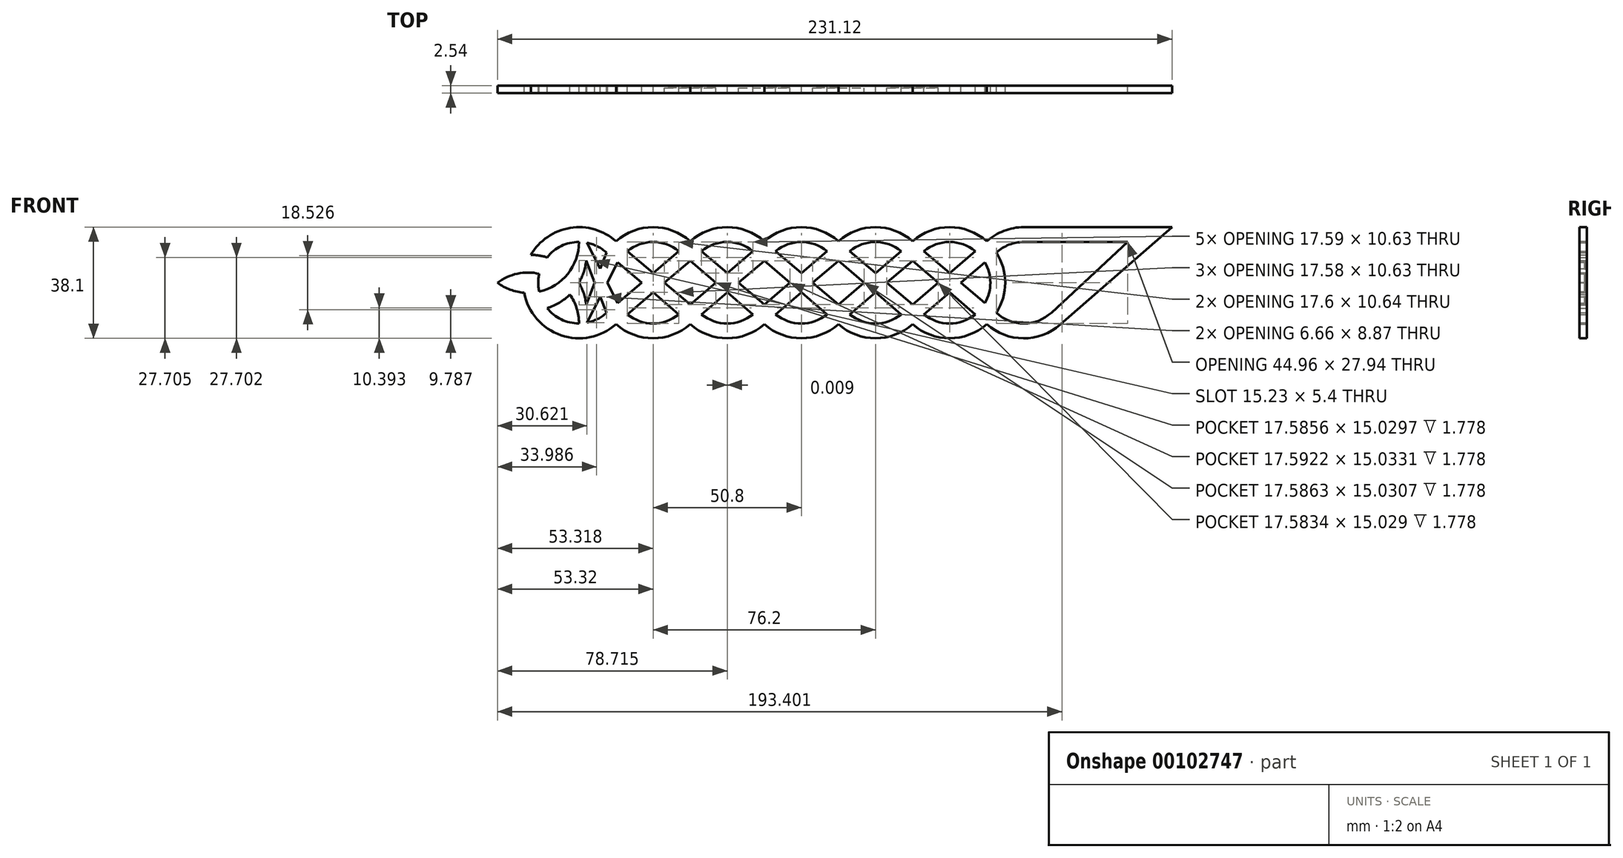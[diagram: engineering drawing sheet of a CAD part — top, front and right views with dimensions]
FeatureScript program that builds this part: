
annotation { "Feature Type Name" : "Feature", "Feature Type Description" : "" }
export const myFeature = defineFeature(function(context is Context, id is Id, definition is map)
    precondition{}
    {
        {
            var Q0;
            Q0=qCreatedBy(makeId("Front.planeOp"),FACE);
            var sketch = newSketch(context, id + "F3", { "sketchPlane" : qUnion([Q0])});
            skPoint(sketch, "E0", {"position": v(0, 0) * mm});
            skLineSegment(sketch, "E1.bottom", {"start": v(0, 0) * mm, "end": v(0, 0) * mm});
            skLineSegment(sketch, "E1.top", {"start": v(0, 0) * mm, "end": v(0, 0) * mm});
            skLineSegment(sketch, "E1.left", {"start": v(0, 0) * mm, "end": v(0, 0) * mm});
            skLineSegment(sketch, "E1.right", {"start": v(0, 0) * mm, "end": v(0, 0) * mm});
            skLineSegment(sketch, "E2.bottom", {"start": v(76.2, 19.05) * mm, "end": v(-76.2, 19.05) * mm, "construction": true});
            skLineSegment(sketch, "E2.top", {"start": v(76.2, -19.05) * mm, "end": v(-76.2, -19.05) * mm, "construction": true});
            skPoint(sketch, "E3", {"position": v(-76.2, 19.05) * mm});
            skPoint(sketch, "E4", {"position": v(76.2, 19.05) * mm});
            skPoint(sketch, "E5", {"position": v(76.2, -19.05) * mm});
            skPoint(sketch, "E6", {"position": v(-76.2, -19.05) * mm});
            skPoint(sketch, "E7", {"position": v(-76.2, 13.97) * mm});
            skPoint(sketch, "E8", {"position": v(-76.2, -13.97) * mm});
            skPoint(sketch, "E9", {"position": v(76.2, -13.97) * mm});
            skPoint(sketch, "E10", {"position": v(-50.8, 19.05) * mm});
            skPoint(sketch, "E11", {"position": v(-25.4, 19.05) * mm});
            skPoint(sketch, "E12", {"position": v(0, 19.05) * mm});
            skPoint(sketch, "E13", {"position": v(25.4, 19.05) * mm});
            skPoint(sketch, "E14", {"position": v(50.8, 19.05) * mm});
            skPoint(sketch, "E15", {"position": v(-50.8, 13.97) * mm});
            skPoint(sketch, "E16", {"position": v(-25.4, 13.97) * mm});
            skPoint(sketch, "E17", {"position": v(0, 13.97) * mm});
            skPoint(sketch, "E18", {"position": v(25.4, 13.97) * mm});
            skPoint(sketch, "E19", {"position": v(50.8, 13.97) * mm});
            skPoint(sketch, "E20", {"position": v(76.2, 13.97) * mm});
            skLineSegment(sketch, "E21", {"start": v(-76.2, 0) * mm, "end": v(-54.7, 0) * mm, "construction": true});
            skPoint(sketch, "E22", {"position": v(-76.2, 0) * mm});
            skPoint(sketch, "E23", {"position": v(76.2, 0) * mm});
            skPoint(sketch, "E24.MirrorP", {"position": v(-50.8, -19.05) * mm});
            skPoint(sketch, "E25.MirrorP", {"position": v(-50.8, -13.97) * mm});
            skPoint(sketch, "E26.MirrorP", {"position": v(-25.4, -19.05) * mm});
            skPoint(sketch, "E27.MirrorP", {"position": v(-25.4, -13.97) * mm});
            skPoint(sketch, "E28.MirrorP", {"position": v(0, -19.05) * mm});
            skPoint(sketch, "E29.MirrorP", {"position": v(0, -13.97) * mm});
            skPoint(sketch, "E30.MirrorP", {"position": v(25.4, -13.97) * mm});
            skPoint(sketch, "E31.MirrorP", {"position": v(25.4, -19.05) * mm});
            skPoint(sketch, "E32.MirrorP", {"position": v(50.8, -13.97) * mm});
            skPoint(sketch, "E33.MirrorP", {"position": v(50.8, -19.05) * mm});
            skPoint(sketch, "E34", {"position": v(-50.8, 0) * mm});
            skPoint(sketch, "E35", {"position": v(-25.4, 0) * mm});
            skPoint(sketch, "E36", {"position": v(25.4, 0) * mm});
            skPoint(sketch, "E37", {"position": v(50.8, 0) * mm});
            skArc(sketch, "E38", {"start": v(-66.8, 10.34) * mm, "mid": v(-70.21, 12.62) * mm, "end": v(-74.14, 13.82) * mm});
            skArc(sketch, "E39", {"start": v(-63.5, -5.82) * mm, "mid": v(-63.2, -6.42) * mm, "end": v(-62.9, -7) * mm, "construction": true});
            skArc(sketch, "E40", {"start": v(-63.75, -13.97) * mm, "mid": v(-50.8, -19.05) * mm, "end": v(-37.85, -13.97) * mm});
            skArc(sketch, "E41", {"start": v(-8.8, -10.86) * mm, "mid": v(0, -13.97) * mm, "end": v(8.8, -10.85) * mm});
            skArc(sketch, "E42", {"start": v(-12.7, -14.2) * mm, "mid": v(0, -19.05) * mm, "end": v(12.7, -14.2) * mm});
            skArc(sketch, "E43", {"start": v(16.6, -10.86) * mm, "mid": v(25.8, -13.96) * mm, "end": v(34.8, -10.34) * mm});
            skArc(sketch, "E44", {"start": v(12.7, -14.2) * mm, "mid": v(25.4, -19.05) * mm, "end": v(38.1, -14.2) * mm});
            skArc(sketch, "E45", {"start": v(42, -10.86) * mm, "mid": v(59.88, -10.62) * mm, "end": v(62.9, 7) * mm});
            skArc(sketch, "E46", {"start": v(38.1, -14.2) * mm, "mid": v(63.18, -14.48) * mm, "end": v(66.8, 10.34) * mm});
            skArc(sketch, "E47", {"start": v(76.2, 13.97) * mm, "mid": v(71.16, 13.03) * mm, "end": v(66.8, 10.34) * mm});
            skArc(sketch, "E48", {"start": v(76.2, 19.05) * mm, "mid": v(69.4, 17.8) * mm, "end": v(63.5, 14.2) * mm});
            skPoint(sketch, "E49", {"position": v(127, 19.05) * mm});
            skLineSegment(sketch, "E50", {"start": v(76.2, 19.05) * mm, "end": v(127, 19.05) * mm});
            skLineSegment(sketch, "E51", {"start": v(127, 19.05) * mm, "end": v(88.73, -14.35) * mm});
            skPoint(sketch, "E52", {"position": v(111.76, 13.97) * mm});
            skLineSegment(sketch, "E53", {"start": v(111.76, 13.97) * mm, "end": v(85.7, -10.23) * mm});
            skLineSegment(sketch, "E54", {"start": v(85.7, -10.23) * mm, "end": v(111.76, 13.97) * mm, "construction": true});
            skLineSegment(sketch, "E55", {"start": v(111.76, 13.97) * mm, "end": v(76.2, 13.97) * mm});
            skPoint(sketch, "E56", {"position": v(-109.2, 0) * mm});
            skPoint(sketch, "E57", {"position": v(-104.12, 0) * mm});
            skPoint(sketch, "E58", {"position": v(-71.12, 18.36) * mm});
            skLineSegment(sketch, "E59.trimOffspring", {"start": v(-63.75, 13.97) * mm, "end": v(-63.25, 13.97) * mm, "construction": true});
            skLineSegment(sketch, "E60", {"start": v(-63.5, -14.2) * mm, "end": v(-50.8, -3.34) * mm});
            skLineSegment(sketch, "E61", {"start": v(-66.8, -10.34) * mm, "end": v(-54.7, 0) * mm});
            skLineSegment(sketch, "E62", {"start": v(-62.9, 7) * mm, "end": v(-42.01, -10.86) * mm});
            skLineSegment(sketch, "E63", {"start": v(-37.78, -14.48) * mm, "end": v(-37.78, -14.48) * mm});
            skLineSegment(sketch, "E64", {"start": v(-38.1, -7.51) * mm, "end": v(-59.6, 10.85) * mm});
            skArc(sketch, "E65.trimOffspring", {"start": v(-63.25, 13.97) * mm, "mid": v(-79.04, 18.84) * mm, "end": v(-92.7, 9.52) * mm});
            skPoint(sketch, "E66.orphan", {"position": v(-71.12, -18.36) * mm});
            skPoint(sketch, "E67.orphan", {"position": v(-63.5, 5.82) * mm});
            skPoint(sketch, "E68.MirrorCS.start.orphan", {"position": v(-63.5, -5.82) * mm});
            skArc(sketch, "E69", {"start": v(-76.2, -13.97) * mm, "mid": v(-77, -8.76) * mm, "end": v(-79.3, -4.03) * mm});
            skArc(sketch, "E70", {"start": v(-76.2, -19.05) * mm, "mid": v(-73.65, -9.52) * mm, "end": v(-76.2, 0) * mm});
            skArc(sketch, "E71.MirrorCS", {"start": v(-76.2, 13.97) * mm, "mid": v(-80.03, 3.06) * mm, "end": v(-89.83, -3.06) * mm});
            skArc(sketch, "E72.MirrorCS", {"start": v(-76.2, 19.05) * mm, "mid": v(-74.97, 2.54) * mm, "end": v(-87.13, -8.7) * mm});
            skLineSegment(sketch, "E73", {"start": v(-76.2, -19.05) * mm, "end": v(-75.31, -17.31) * mm, "construction": true});
            skLineSegment(sketch, "E74", {"start": v(-73.74, -7.62) * mm, "end": v(-70.8, 0) * mm});
            skLineSegment(sketch, "E75", {"start": v(-62.9, -7) * mm, "end": v(-73.47, 13.7) * mm});
            skLineSegment(sketch, "E76", {"start": v(-66.8, -10.34) * mm, "end": v(-73.74, 7.62) * mm});
            skLineSegment(sketch, "E77", {"start": v(-12.45, 14.42) * mm, "end": v(-25.4, 3.34) * mm});
            skLineSegment(sketch, "E78", {"start": v(-41.4, -10.34) * mm, "end": v(-41.4, -10.34) * mm});
            skLineSegment(sketch, "E79", {"start": v(-38.12, -14.22) * mm, "end": v(-25.4, -3.34) * mm});
            skArc(sketch, "E80.trimOffspring", {"start": v(-38.1, 14.2) * mm, "mid": v(-53.34, 18.88) * mm, "end": v(-66.8, 10.34) * mm});
            skArc(sketch, "E81.trimOffspring", {"start": v(-38.1, -14.2) * mm, "mid": v(-25.4, -19.05) * mm, "end": v(-12.7, -14.2) * mm});
            skLineSegment(sketch, "E82", {"start": v(-34.2, 10.85) * mm, "end": v(-12.7, -7.52) * mm});
            skLineSegment(sketch, "E83", {"start": v(12.45, 13.97) * mm, "end": v(0, 3.33) * mm});
            skLineSegment(sketch, "E84", {"start": v(-8.8, 10.85) * mm, "end": v(12.7, -7.52) * mm});
            skLineSegment(sketch, "E85", {"start": v(-12.7, 7.52) * mm, "end": v(8.8, -10.85) * mm});
            skArc(sketch, "E86.trimOffspring", {"start": v(-9.4, 10.34) * mm, "mid": v(-9.4, 10.34) * mm, "end": v(-9.4, 10.34) * mm, "construction": true});
            skArc(sketch, "E87.trimOffspring", {"start": v(-34.2, -10.86) * mm, "mid": v(-25.04, -13.97) * mm, "end": v(-16.05, -10.38) * mm});
            skArc(sketch, "E88.trimOffspring", {"start": v(-16.61, 10.86) * mm, "mid": v(-25.8, 13.96) * mm, "end": v(-34.8, 10.34) * mm});
            skArc(sketch, "E89.trimOffspring", {"start": v(-12.7, 14.2) * mm, "mid": v(-25.57, 19.05) * mm, "end": v(-38.35, 13.97) * mm});
            skLineSegment(sketch, "E90", {"start": v(16, 10.34) * mm, "end": v(3.9, 0) * mm});
            skArc(sketch, "E91.trimOffspring", {"start": v(38.1, 14.2) * mm, "mid": v(25.23, 19.05) * mm, "end": v(12.45, 13.97) * mm});
            skArc(sketch, "E92.trimOffspring", {"start": v(34.19, 10.86) * mm, "mid": v(25, 13.96) * mm, "end": v(16, 10.34) * mm});
            skArc(sketch, "E93.trimOffspring", {"start": v(8.8, 10.85) * mm, "mid": v(-0.4, 13.96) * mm, "end": v(-9.4, 10.34) * mm});
            skArc(sketch, "E94.trimOffspring", {"start": v(12.7, 14.2) * mm, "mid": v(-0.17, 19.05) * mm, "end": v(-12.95, 13.97) * mm});
            skLineSegment(sketch, "E95", {"start": v(8.8, -10.85) * mm, "end": v(21.5, 0) * mm});
            skLineSegment(sketch, "E96", {"start": v(41.4, 10.34) * mm, "end": v(29.31, 0) * mm});
            skLineSegment(sketch, "E97", {"start": v(12.7, 7.52) * mm, "end": v(34.2, -10.85) * mm});
            skLineSegment(sketch, "E98", {"start": v(16.6, 10.86) * mm, "end": v(38.1, -7.51) * mm});
            skLineSegment(sketch, "E99", {"start": v(63.5, 14.2) * mm, "end": v(50.8, 3.34) * mm});
            skLineSegment(sketch, "E100.trimOffspring", {"start": v(63.25, -13.97) * mm, "end": v(63.75, -13.97) * mm, "construction": true});
            skLineSegment(sketch, "E101", {"start": v(66.8, 10.34) * mm, "end": v(54.71, 0) * mm});
            skArc(sketch, "E102.trimOffspring", {"start": v(63.25, -13.97) * mm, "mid": v(75.91, -19.05) * mm, "end": v(88.73, -14.35) * mm});
            skArc(sketch, "E103.trimOffspring", {"start": v(66.8, -10.34) * mm, "mid": v(76.28, -13.97) * mm, "end": v(85.7, -10.23) * mm});
            skLineSegment(sketch, "E104", {"start": v(42, 10.86) * mm, "end": v(62.9, -7) * mm});
            skLineSegment(sketch, "E105", {"start": v(38.1, 7.52) * mm, "end": v(59.6, -10.85) * mm});
            skArc(sketch, "E106.trimOffspring", {"start": v(-74.14, -13.82) * mm, "mid": v(-70.21, -12.62) * mm, "end": v(-66.8, -10.34) * mm});
            skArc(sketch, "E107.trimOffspring", {"start": v(-76.2, 13.97) * mm, "mid": v(-82.27, 12.58) * mm, "end": v(-87.13, 8.7) * mm});
            skArc(sketch, "E108.trimOffspring", {"start": v(-94.94, 3.44) * mm, "mid": v(-85.37, -16.7) * mm, "end": v(-63.25, -13.97) * mm});
            skArc(sketch, "E109.trimOffspring", {"start": v(-89.83, 3.06) * mm, "mid": v(-87.1, -8.73) * mm, "end": v(-76.2, -13.97) * mm});
            skArc(sketch, "E110.trimOffspring", {"start": v(-94.94, -3.44) * mm, "mid": v(-99.77, -2.38) * mm, "end": v(-104.12, 0) * mm});
            skArc(sketch, "E111.trimOffspring", {"start": v(-92.7, -9.53) * mm, "mid": v(-102.22, -6.97) * mm, "end": v(-109.2, 0) * mm});
            skArc(sketch, "E112.trimOffspring", {"start": v(-83.2, 0) * mm, "mid": v(-93.65, 3.48) * mm, "end": v(-104.12, 0) * mm});
            skArc(sketch, "E113.trimOffspring", {"start": v(-79.3, 4.03) * mm, "mid": v(-95.24, 9.35) * mm, "end": v(-109.2, 0) * mm});
            skLineSegment(sketch, "E114.trimOffspring", {"start": v(-68.93, 4.83) * mm, "end": v(-66.8, 10.34) * mm});
            skLineSegment(sketch, "E115.trimOffspring", {"start": v(-66.47, 0) * mm, "end": v(-62.9, 7) * mm});
            skPoint(sketch, "E116.orphan", {"position": v(-66.8, -10.34) * mm});
            skArc(sketch, "E117.trimOffspring", {"start": v(-59.6, -10.86) * mm, "mid": v(-50.4, -13.96) * mm, "end": v(-41.4, -10.34) * mm});
            skLineSegment(sketch, "E118.trimOffspring", {"start": v(-50.8, 3.33) * mm, "end": v(-38.35, 13.97) * mm});
            skLineSegment(sketch, "E119.trimOffspring", {"start": v(-46.9, 0) * mm, "end": v(-34.8, 10.34) * mm});
            skLineSegment(sketch, "E120.trimOffspring", {"start": v(-46.9, 0) * mm, "end": v(-29.3, 0) * mm, "construction": true});
            skLineSegment(sketch, "E121.trimOffspring", {"start": v(-37.85, -13.97) * mm, "end": v(-37.83, -13.97) * mm, "construction": true});
            skLineSegment(sketch, "E122.trimOffspring", {"start": v(-63.75, -13.97) * mm, "end": v(-63.23, -13.97) * mm, "construction": true});
            skLineSegment(sketch, "E123.trimOffspring", {"start": v(-73.47, -13.7) * mm, "end": v(-68.93, -4.83) * mm});
            skLineSegment(sketch, "E124.trimOffspring", {"start": v(-75.31, 17.31) * mm, "end": v(-76.2, 19.05) * mm, "construction": true});
            skLineSegment(sketch, "E125.trimOffspring", {"start": v(-38.1, 7.52) * mm, "end": v(-16.6, -10.85) * mm});
            skArc(sketch, "E126.trimOffspring", {"start": v(-42, 10.85) * mm, "mid": v(-53.34, 13.74) * mm, "end": v(-62.9, 7) * mm});
            skLineSegment(sketch, "E127.trimOffspring", {"start": v(-29.3, 0) * mm, "end": v(-41.4, -10.34) * mm});
            skLineSegment(sketch, "E128.trimOffspring", {"start": v(-21.5, 0) * mm, "end": v(21.5, 0) * mm, "construction": true});
            skLineSegment(sketch, "E129.trimOffspring", {"start": v(-21.5, 0) * mm, "end": v(-9.4, 10.34) * mm});
            skLineSegment(sketch, "E130.trimOffspring", {"start": v(-38.1, -14.2) * mm, "end": v(-37.78, -14.48) * mm, "construction": true});
            skLineSegment(sketch, "E131.trimOffspring", {"start": v(-3.9, 0) * mm, "end": v(-16.6, -10.85) * mm});
            skLineSegment(sketch, "E132.trimOffspring", {"start": v(0, -3.34) * mm, "end": v(-12.7, -14.2) * mm});
            skLineSegment(sketch, "E133.trimOffspring", {"start": v(25.4, 3.34) * mm, "end": v(38.1, 14.2) * mm});
            skLineSegment(sketch, "E134.trimOffspring", {"start": v(29.31, 0) * mm, "end": v(46.9, 0) * mm, "construction": true});
            skLineSegment(sketch, "E135.trimOffspring", {"start": v(25.4, -3.34) * mm, "end": v(12.7, -14.2) * mm});
            skLineSegment(sketch, "E136.trimOffspring", {"start": v(46.9, 0) * mm, "end": v(34.8, -10.34) * mm});
            skLineSegment(sketch, "E137.trimOffspring", {"start": v(50.8, -3.34) * mm, "end": v(38.1, -14.2) * mm});
            skArc(sketch, "E138.trimOffspring", {"start": v(59.6, 10.86) * mm, "mid": v(50.4, 13.96) * mm, "end": v(41.4, 10.34) * mm});
            skArc(sketch, "E139.trimOffspring", {"start": v(63.5, 14.2) * mm, "mid": v(50.8, 19.05) * mm, "end": v(38.1, 14.2) * mm});
            skPoint(sketch, "E140.orphan", {"position": v(-12.45, 13.97) * mm});
            skSolve(sketch);
        }
        {
            var Q0;
            {var subQ6=sQuery(id+"F3.wireOp",EDGE,"E47");Q0=makeQuery(id+"F3.imprint","IMPRINT",FACE,{"disambiguationData":[TD([[makeQuery(id+"F3.imprint","IMPRINT",EDGE,{"derivedFrom":subQ6}),-1.0]])]});}
            var Q1;
            {var subQ0=sQuery(id+"F3.wireOp",EDGE,"E137.trimOffspring");var subQ5=sQuery(id+"F3.wireOp",EDGE,"E45");var subQ9=makeQuery(id+"F3.imprint","INTERSECT",VERTEX,{"derivedFrom":[subQ5,subQ0]});Q1=makeQuery(id+"F3.imprint","IMPRINT",FACE,{"disambiguationData":[TD([[makeQuery(id+"F3.imprint","IMPRINT",EDGE,{"disambiguationData":[TD([[subQ9,-1.0]])],"derivedFrom":subQ5}),-1.0]])]});}
            var Q2;
            {var subQ0=sQuery(id+"F3.wireOp",EDGE,"E104");var subQ9=sQuery(id+"F3.wireOp",EDGE,"E45");var subQ10=makeQuery(id+"F3.imprint","INTERSECT",VERTEX,{"derivedFrom":[subQ9,subQ0]});Q2=makeQuery(id+"F3.imprint","IMPRINT",FACE,{"disambiguationData":[TD([[makeQuery(id+"F3.imprint","IMPRINT",EDGE,{"disambiguationData":[TD([[subQ10,1.0]])],"derivedFrom":subQ9}),1.0]])]});}
            var Q3;
            {var subQ13=sQuery(id+"F3.wireOp",EDGE,"E139.trimOffspring");Q3=makeQuery(id+"F3.imprint","IMPRINT",FACE,{"disambiguationData":[TD([[makeQuery(id+"F3.imprint","IMPRINT",EDGE,{"derivedFrom":subQ13}),1.0]])]});}
            var Q4;
            {var subQ5=sQuery(id+"F3.wireOp",EDGE,"E44");Q4=makeQuery(id+"F3.imprint","IMPRINT",FACE,{"disambiguationData":[TD([[makeQuery(id+"F3.imprint","IMPRINT",EDGE,{"derivedFrom":subQ5}),1.0]])]});}
            var Q5;
            {var subQ4=sQuery(id+"F3.wireOp",EDGE,"E136.trimOffspring");var subQ5=sQuery(id+"F3.wireOp",EDGE,"E43");var subQ6=makeQuery(id+"F3.imprint","INTERSECT",VERTEX,{"derivedFrom":[subQ5,subQ4]});Q5=makeQuery(id+"F3.imprint","IMPRINT",FACE,{"disambiguationData":[TD([[makeQuery(id+"F3.imprint","IMPRINT",EDGE,{"disambiguationData":[TD([[subQ6,1.0]])],"derivedFrom":subQ5}),1.0]])]});}
            var Q6;
            {var subQ1=sQuery(id+"F3.wireOp",EDGE,"E83");var subQ11=sQuery(id+"F3.wireOp",EDGE,"E91.trimOffspring");var subQ13=makeQuery(id+"F3.imprint","INTERSECT",VERTEX,{"derivedFrom":[subQ1,subQ11]});Q6=makeQuery(id+"F3.imprint","IMPRINT",FACE,{"disambiguationData":[TD([[makeQuery(id+"F3.imprint","IMPRINT",EDGE,{"disambiguationData":[TD([[subQ13,-1.0]])],"derivedFrom":subQ1}),1.0]])]});}
            var Q7;
            {var subQ4=sQuery(id+"F3.wireOp",EDGE,"E41");Q7=makeQuery(id+"F3.imprint","IMPRINT",FACE,{"disambiguationData":[TD([[makeQuery(id+"F3.imprint","IMPRINT",EDGE,{"derivedFrom":subQ4}),-1.0]])]});}
            var Q8;
            {var subQ0=sQuery(id+"F3.wireOp",EDGE,"E87.trimOffspring");var subQ1=sQuery(id+"F3.wireOp",EDGE,"E79");var subQ2=makeQuery(id+"F3.imprint","INTERSECT",VERTEX,{"derivedFrom":[subQ1,subQ0]});Q8=makeQuery(id+"F3.imprint","IMPRINT",FACE,{"disambiguationData":[TD([[makeQuery(id+"F3.imprint","IMPRINT",EDGE,{"disambiguationData":[TD([[subQ2,1.0]])],"derivedFrom":subQ1}),-1.0]])]});}
            var Q9;
            {var subQ9=sQuery(id+"F3.wireOp",EDGE,"E77");var subQ17=makeQuery(id+"F3.imprint","INTERSECT",VERTEX,{"derivedFrom":[subQ9,sQuery(id+"F3.wireOp",EDGE,"E88.trimOffspring")]});Q9=makeQuery(id+"F3.imprint","IMPRINT",FACE,{"disambiguationData":[TD([[makeQuery(id+"F3.imprint","IMPRINT",EDGE,{"disambiguationData":[TD([[subQ17,1.0]])],"derivedFrom":subQ9}),1.0]])]});}
            var Q10;
            {var subQ4=sQuery(id+"F3.wireOp",EDGE,"E118.trimOffspring");var subQ5=sQuery(id+"F3.wireOp",EDGE,"E64");var subQ6=makeQuery(id+"F3.imprint","INTERSECT",VERTEX,{"derivedFrom":[subQ5,subQ4]});Q10=makeQuery(id+"F3.imprint","IMPRINT",FACE,{"disambiguationData":[TD([[makeQuery(id+"F3.imprint","IMPRINT",EDGE,{"disambiguationData":[TD([[subQ6,1.0]])],"derivedFrom":subQ5}),-1.0]])]});}
            var Q11;
            {var subQ9=sQuery(id+"F3.wireOp",EDGE,"E79");var subQ13=sQuery(id+"F3.wireOp",EDGE,"E40");var subQ17=makeQuery(id+"F3.imprint","INTERSECT",VERTEX,{"derivedFrom":[subQ13,subQ9]});Q11=makeQuery(id+"F3.imprint","IMPRINT",FACE,{"disambiguationData":[TD([[makeQuery(id+"F3.imprint","IMPRINT",EDGE,{"disambiguationData":[TD([[subQ17,-1.0]])],"derivedFrom":subQ13}),1.0]])]});}
            var Q12;
            {var subQ4=sQuery(id+"F3.wireOp",EDGE,"E62");var subQ5=makeQuery(id+"F3.imprint","INTERSECT",VERTEX,{"derivedFrom":[sQuery(id+"F3.wireOp",EDGE,"E60"),subQ4]});Q12=makeQuery(id+"F3.imprint","IMPRINT",FACE,{"disambiguationData":[TD([[makeQuery(id+"F3.imprint","IMPRINT",EDGE,{"disambiguationData":[TD([[subQ5,1.0]])],"derivedFrom":subQ4}),1.0]])]});}
            var Q13;
            {var subQ0=sQuery(id+"F3.wireOp",EDGE,"E114.trimOffspring");Q13=makeQuery(id+"F3.imprint","IMPRINT",FACE,{"disambiguationData":[TD([[makeQuery(id+"F3.imprint","IMPRINT",EDGE,{"derivedFrom":subQ0}),-1.0]])]});}
            var Q14;
            {var subQ2=sQuery(id+"F3.wireOp",EDGE,"E62");var subQ6=sQuery(id+"F3.wireOp",EDGE,"E60");var subQ7=makeQuery(id+"F3.imprint","INTERSECT",VERTEX,{"derivedFrom":[subQ6,subQ2]});Q14=makeQuery(id+"F3.imprint","IMPRINT",FACE,{"disambiguationData":[TD([[makeQuery(id+"F3.imprint","IMPRINT",EDGE,{"disambiguationData":[TD([[subQ7,1.0]])],"derivedFrom":subQ6}),1.0]])]});}
            var Q15;
            {var subQ4=sQuery(id+"F3.wireOp",EDGE,"E72.MirrorCS");var subQ5=sQuery(id+"F3.wireOp",EDGE,"E38");var subQ6=makeQuery(id+"F3.imprint","INTERSECT",VERTEX,{"derivedFrom":[subQ5,subQ4]});Q15=makeQuery(id+"F3.imprint","IMPRINT",FACE,{"disambiguationData":[TD([[makeQuery(id+"F3.imprint","IMPRINT",EDGE,{"disambiguationData":[TD([[subQ6,1.0]])],"derivedFrom":subQ5}),1.0]])]});}
            var Q16;
            {var subQ0=sQuery(id+"F3.wireOp",EDGE,"E74");Q16=makeQuery(id+"F3.imprint","IMPRINT",FACE,{"disambiguationData":[TD([[makeQuery(id+"F3.imprint","IMPRINT",EDGE,{"derivedFrom":subQ0}),-1.0]])]});}
            var Q17;
            {var subQ0=sQuery(id+"F3.wireOp",EDGE,"E72.MirrorCS");var subQ1=sQuery(id+"F3.wireOp",EDGE,"E38");var subQ2=makeQuery(id+"F3.imprint","INTERSECT",VERTEX,{"derivedFrom":[subQ1,subQ0]});Q17=makeQuery(id+"F3.imprint","IMPRINT",FACE,{"disambiguationData":[TD([[makeQuery(id+"F3.imprint","IMPRINT",EDGE,{"disambiguationData":[TD([[subQ2,1.0]])],"derivedFrom":subQ1}),-1.0]])]});}
            var Q18;
            {var subQ0=sQuery(id+"F3.wireOp",EDGE,"E107.trimOffspring");Q18=makeQuery(id+"F3.imprint","IMPRINT",FACE,{"disambiguationData":[TD([[makeQuery(id+"F3.imprint","IMPRINT",EDGE,{"derivedFrom":subQ0}),-1.0]])]});}
            var Q19;
            {var subQ10=sQuery(id+"F3.wireOp",EDGE,"E69");Q19=makeQuery(id+"F3.imprint","IMPRINT",FACE,{"disambiguationData":[TD([[makeQuery(id+"F3.imprint","IMPRINT",EDGE,{"derivedFrom":subQ10}),-1.0]])]});}
            var Q20;
            {var subQ1=sQuery(id+"F3.wireOp",EDGE,"E110.trimOffspring");Q20=makeQuery(id+"F3.imprint","IMPRINT",FACE,{"disambiguationData":[TD([[makeQuery(id+"F3.imprint","IMPRINT",EDGE,{"derivedFrom":subQ1}),1.0]])]});}
            extrude(context, id + "F0", {"entities" : qUnion([Q0, Q1, Q2, Q3, Q4, Q5, Q6, Q7, Q8, Q9, Q10, Q11, Q12, Q13, Q14, Q15, Q16, Q17, Q18, Q19, Q20]), "depth" : 2.54 * mm});
        }
        {
            var Q0;
            {var subQ1=sQuery(id+"F3.wireOp",EDGE,"E82");var subQ11=makeQuery(id+"F3.imprint","INTERSECT",VERTEX,{"derivedFrom":[sQuery(id+"F3.wireOp",EDGE,"E77"),subQ1]});Q0=makeQuery(id+"F3.imprint","IMPRINT",FACE,{"disambiguationData":[TD([[makeQuery(id+"F3.imprint","IMPRINT",EDGE,{"disambiguationData":[TD([[subQ11,1.0]])],"derivedFrom":subQ1}),-1.0]])]});}
            extrude(context, id + "F1", {"entities" : qUnion([Q0]), "operationType" : NewBodyOperationType.ADD, "depth" : 2.54 * mm});
        }
        {
            var Q0;
            {var subQ0=sQuery(id+"F3.wireOp",EDGE,"E98");var subQ1=sQuery(id+"F3.wireOp",EDGE,"E96");var subQ2=makeQuery(id+"F3.imprint","INTERSECT",VERTEX,{"derivedFrom":[subQ1,subQ0]});Q0=makeQuery(id+"F3.imprint","IMPRINT",FACE,{"disambiguationData":[TD([[makeQuery(id+"F3.imprint","IMPRINT",EDGE,{"disambiguationData":[TD([[subQ2,1.0]])],"derivedFrom":subQ1}),1.0]])]});}
            var Q1;
            {var subQ0=sQuery(id+"F3.wireOp",EDGE,"E127.trimOffspring");var subQ1=sQuery(id+"F3.wireOp",EDGE,"E64");var subQ2=makeQuery(id+"F3.imprint","INTERSECT",VERTEX,{"derivedFrom":[subQ1,subQ0]});Q1=makeQuery(id+"F3.imprint","IMPRINT",FACE,{"disambiguationData":[TD([[makeQuery(id+"F3.imprint","IMPRINT",EDGE,{"disambiguationData":[TD([[subQ2,-1.0]])],"derivedFrom":subQ1}),-1.0]])]});}
            var Q2;
            {var subQ0=sQuery(id+"F3.wireOp",EDGE,"E95");var subQ1=sQuery(id+"F3.wireOp",EDGE,"E84");var subQ2=makeQuery(id+"F3.imprint","INTERSECT",VERTEX,{"derivedFrom":[subQ1,subQ0]});Q2=makeQuery(id+"F3.imprint","IMPRINT",FACE,{"disambiguationData":[TD([[makeQuery(id+"F3.imprint","IMPRINT",EDGE,{"disambiguationData":[TD([[subQ2,1.0]])],"derivedFrom":subQ1}),1.0]])]});}
            var Q3;
            {var subQ0=sQuery(id+"F3.wireOp",EDGE,"E131.trimOffspring");var subQ1=sQuery(id+"F3.wireOp",EDGE,"E82");var subQ2=makeQuery(id+"F3.imprint","INTERSECT",VERTEX,{"derivedFrom":[subQ1,subQ0]});Q3=makeQuery(id+"F3.imprint","IMPRINT",FACE,{"disambiguationData":[TD([[makeQuery(id+"F3.imprint","IMPRINT",EDGE,{"disambiguationData":[TD([[subQ2,1.0]])],"derivedFrom":subQ1}),1.0]])]});}
            extrude(context, id + "F2", {"entities" : qUnion([Q0, Q1, Q2, Q3]), "operationType" : NewBodyOperationType.ADD, "depth" : 0.76 * mm});
        }
    });
